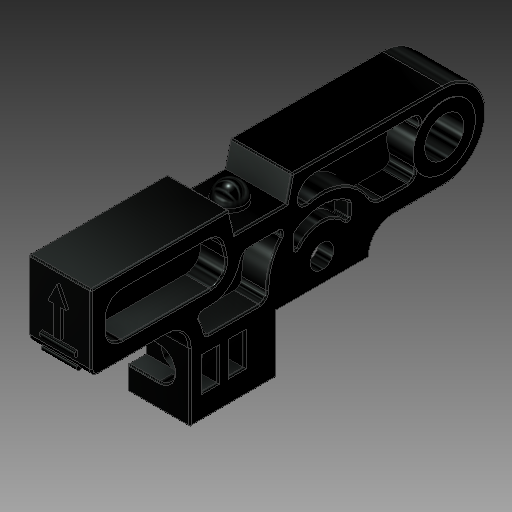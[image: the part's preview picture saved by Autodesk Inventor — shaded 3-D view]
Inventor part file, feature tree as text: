
AUTODESK INVENTOR PART (.ipt)
format: ipt  version: 2018 (Build 220112000, 112)  size: 792,576 bytes
history: native  units: in
note: dims shown in document units (in); Inventor stores cm internally (conversion verified against a paired STEP export)
features: extrude x14, sketch x14, fillet x6, projected_geometry x6, mirror x1
ambient origin geometry x8: Origin, YZ Plane, XZ Plane, XY Plane, X Axis, Y Axis, Z Axis, Center Point
bodies: Solid1 (feature_tree)
feature tree (41):
  extrude  "Extrusion1"  Depth=0.4331in
  extrude  "Extrusion2"  Depth=0.3858in
  extrude  "Extrusion3"  Depth=0.4961in
  fillet  "Fillet1"  Radius=0.8465in
  extrude  "Extrusion4"  Depth=0.5512in
  extrude  "Extrusion5"  Depth=0.0394in
  extrude  "Extrusion6"  Depth=0.315in
  fillet  "Fillet2"  Radius=0.315in
  extrude  "Extrusion7"  Depth=0.1181in
  extrude  "Extrusion8"  Depth=0.1496in
  extrude  "Extrusion9"  Depth=0.0748in
  extrude  "Extrusion10"  Depth=0.2165in
  extrude  "Extrusion11"  Depth=0.0945in TaperAngle=0.0deg
  fillet  "Fillet3"  Radius=0.4331in
  fillet  "Fillet4"  Radius=0.1693in
  fillet  "Fillet5"  Radius=0.3071in
  extrude  "Extrusion12"  Depth=0.1693in TaperAngle=0.0deg
  mirror  "Mirror1"
  fillet  "Fillet6"  Radius=0.0098in
  extrude  "Extrusion13"  Depth=0.4291in
  extrude  "Extrusion14"  Depth=0.1575in
  sketch  "Sketch1"  dims[d0=0.1969in d1=0.4331in]
  sketch  "Sketch2"  dims[d2=1.7717in d3=0.3858in]
  sketch  "Sketch3"  dims[d4=0.4331in d6=0.4961in d8=0.8465in]
  projected_geometry  "Projected Loop1"
  sketch  "Sketch4"  dims[d9=0.5512in d10=0.9055in]
  sketch  "Sketch5"  dims[d12=0.1181in d13=0.0394in]
  sketch  "Sketch6"  dims[d14=0.315in d15=0.0in d16=0.9173in d17=0.315in]
  sketch  "Sketch7"  dims[d18=0.2598in d19=0.1181in]
  projected_geometry  "Projected Loop2"
  sketch  "Sketch8"  dims[d20=0.315in d21=0.0in d22=0.1496in]
  sketch  "Sketch9"  dims[d23=0.0945in d24=0.0in d25=0.0748in]
  projected_geometry  "Projected Loop3"
  sketch  "Sketch10"  dims[d26=0.6102in d27=0.2165in]
  projected_geometry  "Projected Loop4"
  sketch  "Sketch11"  dims[d28=0.1181in d29=0.0945in d30=0.0in d31=0.4331in d32=0.1693in d33=0.0in d34=0.3071in]
  projected_geometry  "Projected Loop5"
  sketch  "Sketch12"  dims[d35=0.2756in d36=0.1693in d37=0.0in d38=0.0098in]
  sketch  "Sketch13"  dims[d39=0.1575in d40=0.4291in]
  sketch  "Sketch14"  dims[d41=0.1693in d42=0.0in d43=0.1575in d44=0.0748in d45=0.0591in d46=0.0748in d47=0.0669in d48=0.1693in d49=0.0in d50=0.0906in d51=0.0906in d52=0.0906in d53=0.0276in d54=0.0276in d55=0.1575in d56=0.1693in d57=0.0in d59=0.1181in d60=0.0787in d61=0.0in d62=0.315in d63=0.0591in d64=0.0984in d65=0.0591in d66=0.0591in d67=0.315in d68=0.0984in d69=0.0787in d71=0.0787in d72=0.0591in d73=0.0591in d74=0.0787in d75=0.0787in d76=0.0787in d77=0.0787in d78=0.128in d79=0.0in d80=0.0787in d81=0.0394in d82=0.0197in d83=0.0039in d84=0.0in d85=0.0079in d86=0.0295in d87=0.0758in d88=0.0295in d89=0.0295in d90=0.0758in d91=1.5748in d93=0.061in d94=0.3937in d96=0.3937in d98=0.1772in d99=0.0in d100=0.0335in d101=0.0906in d102=0.0472in d103=0.1378in d104=0.2835in d105=0.0148in d106=0.0in]
  projected_geometry  "Projected Loop6"
